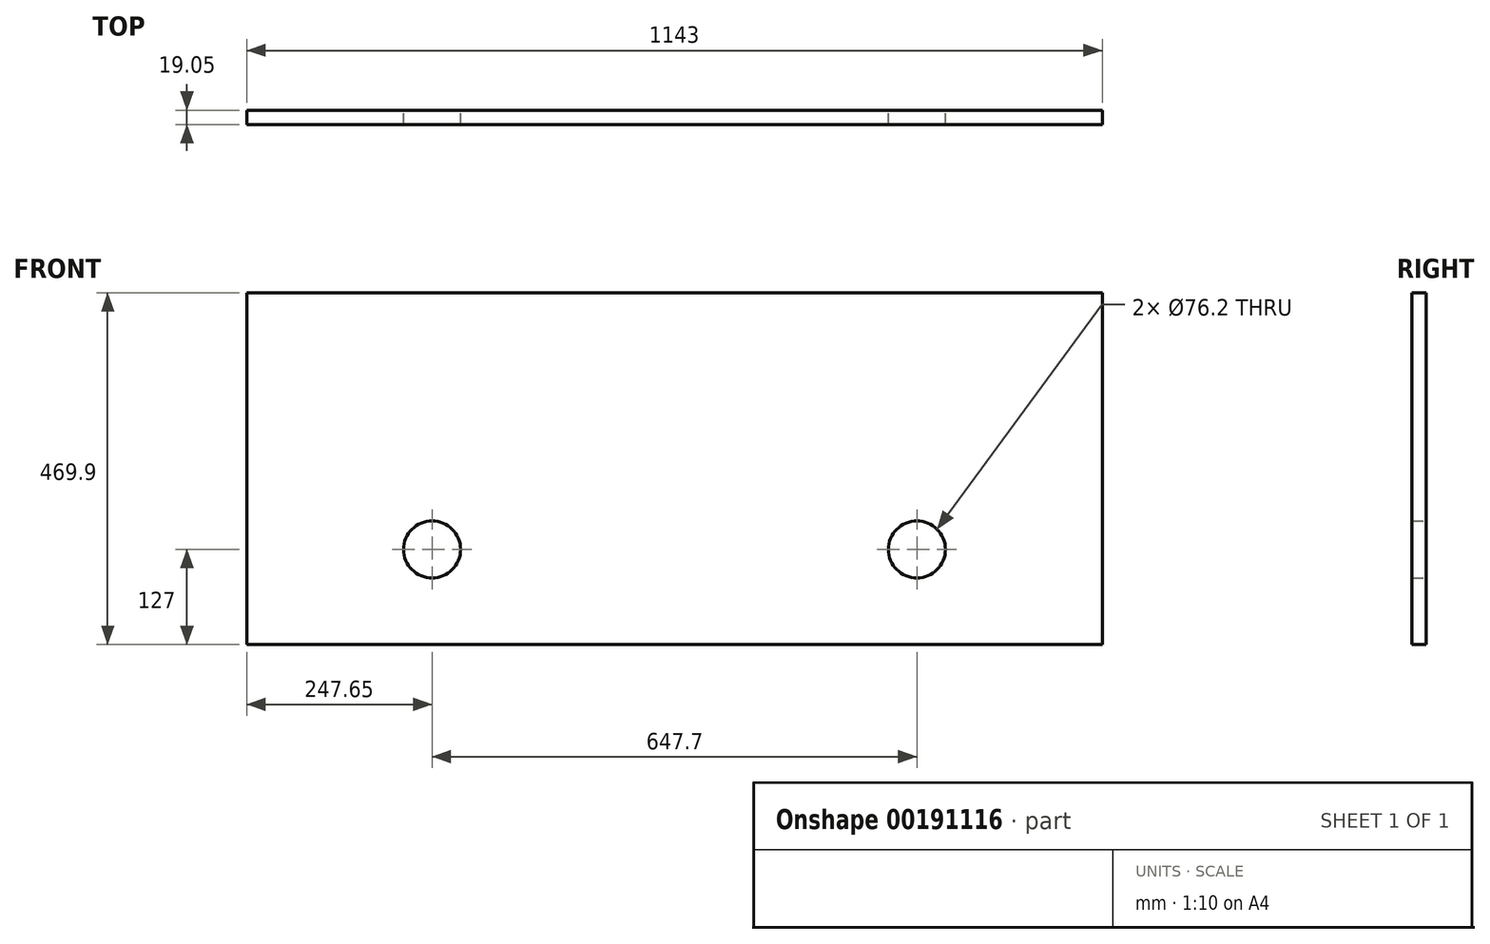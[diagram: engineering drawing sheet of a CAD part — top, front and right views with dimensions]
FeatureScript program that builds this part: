
annotation { "Feature Type Name" : "Feature", "Feature Type Description" : "" }
export const myFeature = defineFeature(function(context is Context, id is Id, definition is map)
    precondition{}
    {
        {
            var Q0;
            Q0=qCreatedBy(makeId("Front.planeOp"),FACE);
            var sketch = newSketch(context, id + "F0", { "sketchPlane" : qUnion([Q0])});
            skLineSegment(sketch, "E0.bottom", {"start": v(571.5, 234.95) * mm, "end": v(-571.5, 234.95) * mm});
            skLineSegment(sketch, "E0.top", {"start": v(571.5, -234.95) * mm, "end": v(-571.5, -234.95) * mm});
            skLineSegment(sketch, "E0.left", {"start": v(571.5, 234.95) * mm, "end": v(571.5, -234.95) * mm});
            skLineSegment(sketch, "E0.right", {"start": v(-571.5, 234.95) * mm, "end": v(-571.5, -234.95) * mm});
            skPoint(sketch, "E0.middle", {"position": v(0, 0) * mm});
            skSolve(sketch);
        }
        {
            var Q0;
            Q0 = qSketchRegion(id + "F0", true);
            extrude(context, id + "F1", {"entities" : qUnion([Q0]), "depth" : 19.05 * mm});
        }
        {
            var Q0;
            Q0=makeQuery(id+"F1.opExtrude","CAP_FACE",FACE,{"disambiguationData":[OSD([sQuery(id+"F0.wireOp",EDGE,"E0.bottom"),sQuery(id+"F0.wireOp",EDGE,"E0.top"),sQuery(id+"F0.wireOp",EDGE,"E0.left"),sQuery(id+"F0.wireOp",EDGE,"E0.right")])],"isStart":true});
            var sketch = newSketch(context, id + "F2", { "sketchPlane" : qUnion([Q0])});
            skCircle(sketch, "E1", {"center": v(-323.85, -107.95) * mm, "radius": 38.1 * mm});
            skCircle(sketch, "E2", {"center": v(323.85, -107.95) * mm, "radius": 38.1 * mm});
            skSolve(sketch);
        }
        {
            var Q0;
            Q0 = qSketchRegion(id + "F2", true);
            extrude(context, id + "F3", {"entities" : qUnion([Q0]), "operationType" : NewBodyOperationType.REMOVE, "endBound" : BoundingType.THROUGH_ALL, "oppositeDirection" : true, "depth" : 25.4 * mm});
        }
    });
